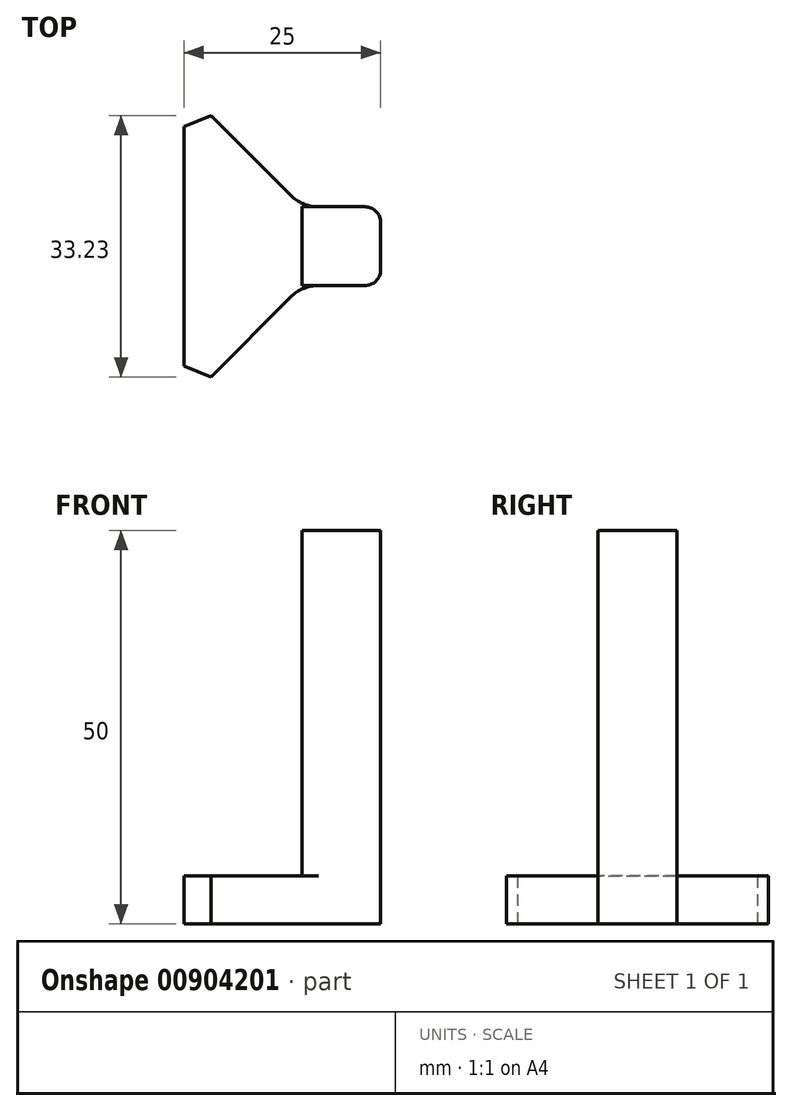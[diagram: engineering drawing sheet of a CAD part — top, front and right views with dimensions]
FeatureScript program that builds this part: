
annotation { "Feature Type Name" : "Feature", "Feature Type Description" : "" }
export const myFeature = defineFeature(function(context is Context, id is Id, definition is map)
    precondition{}
    {
        {
            var Q0;
            Q0=qCreatedBy(makeId("Front.planeOp"),FACE);
            var sketch = newSketch(context, id + "F0", { "sketchPlane" : qUnion([Q0])});
            skLineSegment(sketch, "E0.bottom", {"start": v(0, 0) * mm, "end": v(10, 0) * mm});
            skLineSegment(sketch, "E0.top", {"start": v(0, 50) * mm, "end": v(10, 50) * mm});
            skLineSegment(sketch, "E0.left", {"start": v(0, 0) * mm, "end": v(0, 50) * mm});
            skLineSegment(sketch, "E0.right", {"start": v(10, 0) * mm, "end": v(10, 50) * mm});
            skLineSegment(sketch, "E1.left", {"start": v(0, 0) * mm, "end": v(0, 8.4) * mm});
            skSolve(sketch);
        }
        {
            var Q0;
            Q0=makeQuery(id+"F0.imprint","IMPRINT",FACE,{"disambiguationData":[TD([[makeQuery(id+"F0.imprint","IMPRINT",EDGE,{"derivedFrom":sQuery(id+"F0.wireOp",EDGE,"E1.bottom")}),-1.0]])]});
            var Q1;
            Q1=makeQuery(id+"F0.imprint","IMPRINT",FACE,{"disambiguationData":[TD([[makeQuery(id+"F0.imprint","IMPRINT",EDGE,{"derivedFrom":sQuery(id+"F0.wireOp",EDGE,"E0.bottom")}),1.0]])]});
            extrude(context, id + "F1", {"entities" : qUnion([Q0, Q1]), "endBound" : BoundingType.SYMMETRIC, "depth" : 10 * mm, "offsetDistance" : 25 * mm});
        }
        {
            var Q0;
            Q0=qCreatedBy(makeId("Top.planeOp"),FACE);
            var sketch = newSketch(context, id + "F2", { "sketchPlane" : qUnion([Q0])});
            skLineSegment(sketch, "E2", {"start": v(0, -5) * mm, "end": v(-15, -20.04) * mm});
            skLineSegment(sketch, "E3", {"start": v(-15, 20.04) * mm, "end": v(0, 5) * mm});
            skLineSegment(sketch, "E4", {"start": v(0, 5) * mm, "end": v(0, -5) * mm});
            skLineSegment(sketch, "E5", {"start": v(-15, -20.04) * mm, "end": v(-15, 20.04) * mm});
            skSolve(sketch);
        }
        {
            var Q0;
            Q0=makeQuery(id+"F2.imprint","IMPRINT",FACE,{"disambiguationData":[TD([[makeQuery(id+"F2.imprint","IMPRINT",EDGE,{"derivedFrom":sQuery(id+"F2.wireOp",EDGE,"E2")}),-1.0]])]});
            extrude(context, id + "F3", {"entities" : qUnion([Q0]), "operationType" : NewBodyOperationType.ADD, "depth" : 6.1 * mm, "offsetDistance" : 25 * mm});
        }
        {
            var Q0;
            Q0=makeQuery(id+"F3.opExtrude","CAP_EDGE",EDGE,{"disambiguationData":[OSD([sQuery(id+"F2.wireOp",EDGE,"E4")])],"isStart":false});
            var Q1;
            Q1=makeQuery(id+"F3.boolean.opBoolean","MERGE",EDGE,{"derivedFrom":[makeQuery(id+"F1.opExtrude","CAP_EDGE",EDGE,{"disambiguationData":[OSD([sQuery(id+"F0.wireOp",EDGE,"E0.left"),sQuery(id+"F0.wireOp",EDGE,"E1.left")])],"isStart":true}),makeQuery(id+"F3.opExtrude","SWEPT_EDGE",EDGE,{"disambiguationData":[OSD([sQuery(id+"F2.wireOp",EDGE,"E3"),sQuery(id+"F2.wireOp",EDGE,"E4")])]})]});
            var Q2;
            Q2=makeQuery(id+"F3.boolean.opBoolean","MERGE",EDGE,{"derivedFrom":[makeQuery(id+"F1.opExtrude","CAP_EDGE",EDGE,{"disambiguationData":[OSD([sQuery(id+"F0.wireOp",EDGE,"E0.left"),sQuery(id+"F0.wireOp",EDGE,"E1.left")])],"isStart":false}),makeQuery(id+"F3.opExtrude","SWEPT_EDGE",EDGE,{"disambiguationData":[OSD([sQuery(id+"F2.wireOp",EDGE,"E2"),sQuery(id+"F2.wireOp",EDGE,"E4")])]})]});
            fillet(context, id + "F4", {"entities" : qUnion([Q0, Q1, Q2]), "radius" : 5 * mm, "tangentPropagation" : true, "allowEdgeOverflow" : false});
        }
        {
            var Q0;
            Q0=makeQuery(id+"F1.opExtrude","CAP_EDGE",EDGE,{"disambiguationData":[OSD([sQuery(id+"F0.wireOp",EDGE,"E0.right")])],"isStart":true});
            var Q1;
            Q1=makeQuery(id+"F1.opExtrude","CAP_EDGE",EDGE,{"disambiguationData":[OSD([sQuery(id+"F0.wireOp",EDGE,"E0.right")])],"isStart":false});
            fillet(context, id + "F5", {"entities" : qUnion([Q0, Q1]), "radius" : 2 * mm, "tangentPropagation" : true, "allowEdgeOverflow" : false});
        }
        {
            var Q0;
            Q0=makeQuery(id+"F3.opExtrude","SWEPT_EDGE",EDGE,{"disambiguationData":[OSD([sQuery(id+"F2.wireOp",EDGE,"E3"),sQuery(id+"F2.wireOp",EDGE,"E5")])]});
            chamfer(context, id + "F6", {"entities" : qUnion([Q0]), "width" : 2 * mm, "tangentPropagation" : true});
        }
        {
            var Q0;
            Q0=makeQuery(id+"F3.opExtrude","SWEPT_EDGE",EDGE,{"disambiguationData":[OSD([sQuery(id+"F2.wireOp",EDGE,"E2"),sQuery(id+"F2.wireOp",EDGE,"E5")])]});
            chamfer(context, id + "F7", {"entities" : qUnion([Q0]), "width" : 2 * mm, "tangentPropagation" : true});
        }
    });
